# Revit family: Building-IEC309Connections-GEWISS-IEC309BTS-10°_FLUSH-MOUNT_SOCKET_20-25V_IP67
name_source: partatom
category: Apparecchi elettrici
units: mm (PartAtom-declared; Revit-internal decimal feet)

## family parameters
Condiviso = No
Host = Superficie
Mantenere orientamento annotazione = Sì
Punto di calcolo locali = Sì
Quota connettore circolare = Usa diametro
Taglio con vuoti quando caricato = No
Tipo di parte = Normale

## types (2) — shared parameters
BLOCCO = B=C
Breaking capacity at 1.1 Un = 20A
Catalogue = BUILDING
Colour: = Violet
Corpo centrale = Default(2)
Electrocod = 2211
FORMULA = 1000 mm  [stored 3.28084 ft]
Flange dimensions (mm) = 85x75
Frequency = 50 - 60 Hz
Glow wire test: = 850 °C (active parts) - 650 °C (passive parts)
IDF = f5045b86-b307-4e8a-94a1-0090521ade02
IDT = 857996395c484e7eb52f0599547146e7
IP degree = IP67
Immagine tipo = <Nessuno>
Insulation resistance = - 10 M?
L = 155 mm
N.poli = 1
Operating temperature: = -25 +40 °C
Permissible overload = 22A
Piastra = Default(2)
Produttore = GEWISS S.p.A.
Prospetto di default = 1219 mm
Rated current (A) = 16
Rated voltage: = 20-25 V
Reference h: = -
SEO = Socket outlet
SPinotto = Default(2)
Shock resistance = IK08
Sportello_visibile = Sì
Spostamento_S = 963 mm
Technical sheet = https://www.gewiss.com
Terminal tightening capacity = 1-2.5mm² flexible cables - 1.5-4mm² rigid cables
Thermo-pressure with ball = 125 °C (active parts) - 80 °C (passive parts)
Total number of operations = -5000
Type of wiring = With screw
Typology = 10° angled flush-mounting socket-outlet
URL = https://www.gewiss.com
Version file RFA = 21.11
Voltaggio = 0 V
W = 115 mm

## per-type parameters (varying)
| type | Descrizione | Modello | No. of poles |
| GW62365 - IP67 10°P.RECEPTACLE 2P 16A 24V N.R | IP67 10°P.RECEPTACLE 2P 16A 24V N.R | GW62365 | 2P |
| GW62366 - IP67 10°P.RECEPTACLE 3P 16A 24V N.R | IP67 10°P.RECEPTACLE 3P 16A 24V N.R | GW62366 | 3P |

note: [stored X ft] marks values corroborated as IEEE doubles in the binary element streams (Revit-internal decimal feet)

## geometry (parser evidence)
native form markers: Sweep x1
no freeform markers — native parametric forms only
